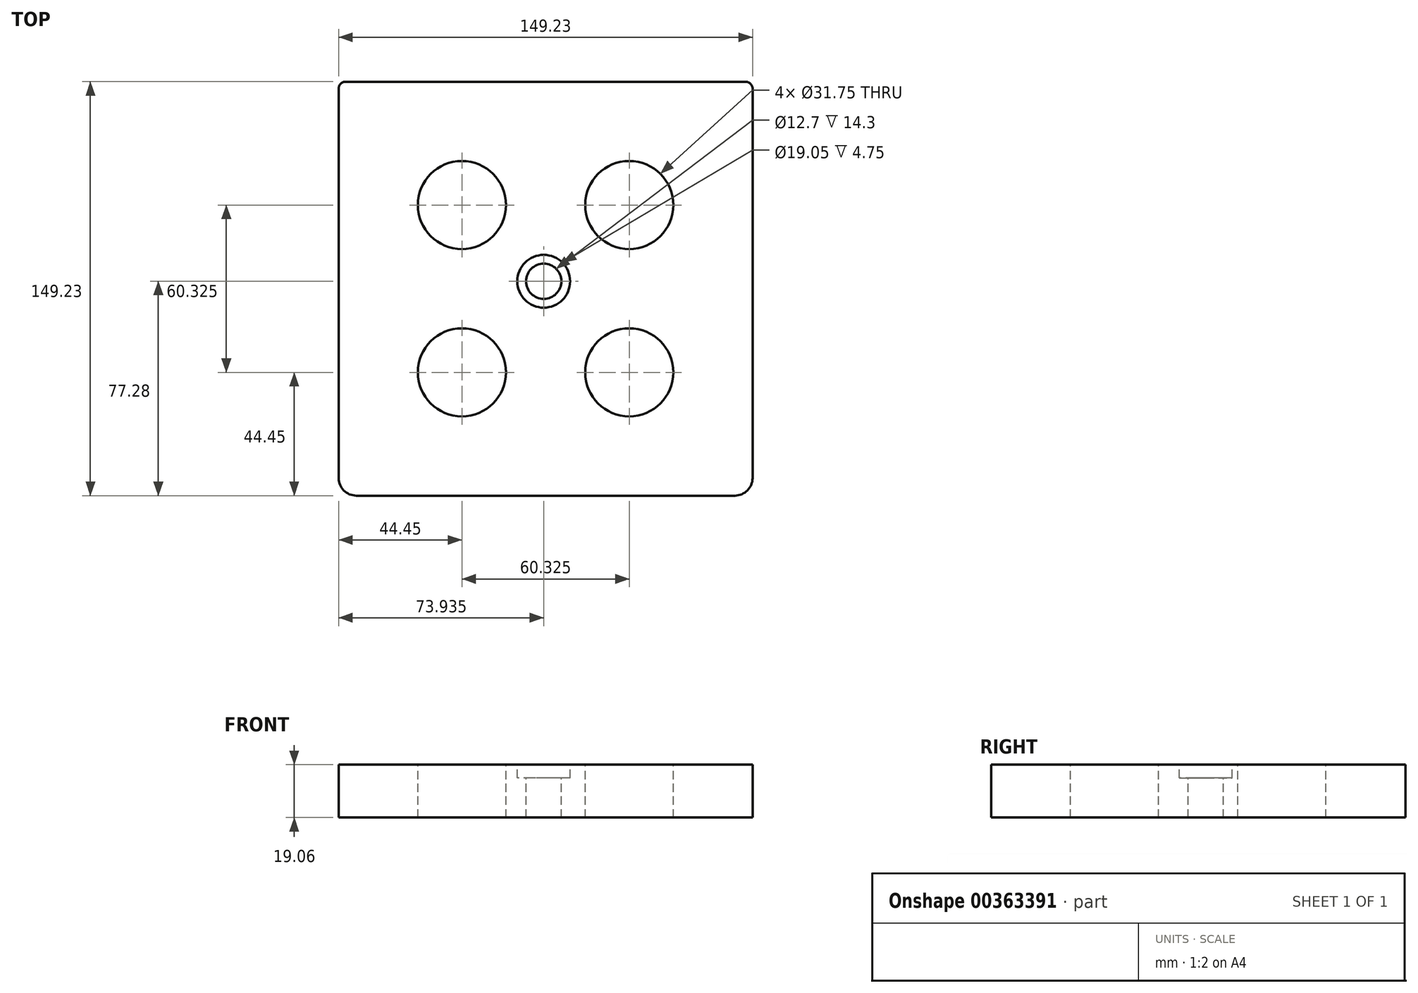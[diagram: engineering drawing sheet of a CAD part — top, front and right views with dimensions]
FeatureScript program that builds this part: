
annotation { "Feature Type Name" : "Feature", "Feature Type Description" : "" }
export const myFeature = defineFeature(function(context is Context, id is Id, definition is map)
    precondition{}
    {
        {
            var Q0;
            Q0=qCreatedBy(makeId("Top.planeOp"),FACE);
            var sketch = newSketch(context, id + "F0", { "sketchPlane" : qUnion([Q0])});
            skLineSegment(sketch, "E0.bottom", {"start": v(69.4, -77.28) * mm, "end": v(-67.12, -77.28) * mm});
            skLineSegment(sketch, "E0.top", {"start": v(73.22, 71.95) * mm, "end": v(-70.93, 71.95) * mm});
            skLineSegment(sketch, "E0.left", {"start": v(75.76, -70.93) * mm, "end": v(75.76, 69.4) * mm});
            skLineSegment(sketch, "E0.right", {"start": v(-73.47, -70.93) * mm, "end": v(-73.47, 69.4) * mm});
            skPoint(sketch, "E1.visualSharp", {"position": v(-73.47, 71.95) * mm});
            skArc(sketch, "E1.filletArc", {"start": v(-70.93, 71.95) * mm, "mid": v(-72.73, 71.2) * mm, "end": v(-73.47, 69.4) * mm});
            skPoint(sketch, "E2.visualSharp", {"position": v(75.76, 71.95) * mm});
            skArc(sketch, "E2.filletArc", {"start": v(75.76, 69.4) * mm, "mid": v(75.01, 71.2) * mm, "end": v(73.22, 71.95) * mm});
            skPoint(sketch, "E3.visualSharp", {"position": v(75.76, -77.28) * mm});
            skArc(sketch, "E3.filletArc", {"start": v(69.4, -77.28) * mm, "mid": v(73.9, -75.42) * mm, "end": v(75.76, -70.93) * mm});
            skPoint(sketch, "E4.visualSharp", {"position": v(-73.47, -77.28) * mm});
            skArc(sketch, "E4.filletArc", {"start": v(-73.47, -70.93) * mm, "mid": v(-71.6, -75.42) * mm, "end": v(-67.12, -77.28) * mm});
            skCircle(sketch, "E5", {"center": v(-29.02, 27.5) * mm, "radius": 15.88 * mm});
            skCircle(sketch, "E6", {"center": v(-29.02, -32.83) * mm, "radius": 15.88 * mm});
            skCircle(sketch, "E7", {"center": v(31.3, -32.83) * mm, "radius": 15.88 * mm});
            skCircle(sketch, "E8", {"center": v(31.3, 27.5) * mm, "radius": 15.88 * mm});
            skSolve(sketch);
        }
        {
            var Q0;
            Q0=makeQuery(id+"F0.imprint","IMPRINT",FACE,{"disambiguationData":[TD([[makeQuery(id+"F0.imprint","IMPRINT",EDGE,{"derivedFrom":sQuery(id+"F0.wireOp",EDGE,"E0.bottom")}),-1.0]])]});
            var Q1;
            Q1=sQuery(id+"F0.wireOp",EDGE,"DEAaRMsh-ce6J-Exax-naJt-bH9Wly1rZSn5");
            extrude(context, id + "F1", {"entities" : qUnion([Q0]), "surfaceEntities" : qUnion([Q1]), "endBound" : BoundingType.SYMMETRIC, "oppositeDirection" : true, "depth" : 19.05 * mm});
        }
        {
            var Q0;
            Q0=makeQuery(id+"F1.opExtrude","CAP_FACE",FACE,{"disambiguationData":[OSD([sQuery(id+"F0.wireOp",EDGE,"E0.bottom"),sQuery(id+"F0.wireOp",EDGE,"E0.top"),sQuery(id+"F0.wireOp",EDGE,"E0.left"),sQuery(id+"F0.wireOp",EDGE,"E0.right"),sQuery(id+"F0.wireOp",EDGE,"E1.filletArc"),sQuery(id+"F0.wireOp",EDGE,"E2.filletArc"),sQuery(id+"F0.wireOp",EDGE,"E3.filletArc"),sQuery(id+"F0.wireOp",EDGE,"E4.filletArc"),sQuery(id+"F0.wireOp",EDGE,"E5"),sQuery(id+"F0.wireOp",EDGE,"E6"),sQuery(id+"F0.wireOp",EDGE,"E7"),sQuery(id+"F0.wireOp",EDGE,"E8")])],"isStart":true});
            var sketch = newSketch(context, id + "F2", { "sketchPlane" : qUnion([Q0])});
            skCircle(sketch, "E9", {"center": v(0.46, 0) * mm, "radius": 6.35 * mm});
            skSolve(sketch);
        }
        {
            var Q0;
            Q0=sQuery(id+"F2.wireOp",VERTEX,"E9.center");
            var Q1;
            Q1=makeQuery(id+"F1.opExtrude","SWEPT_BODY",BODY,{"disambiguationData":[OSD([sQuery(id+"F0.wireOp",EDGE,"E0.bottom"),sQuery(id+"F0.wireOp",EDGE,"E0.top"),sQuery(id+"F0.wireOp",EDGE,"E0.left"),sQuery(id+"F0.wireOp",EDGE,"E0.right"),sQuery(id+"F0.wireOp",EDGE,"E1.filletArc"),sQuery(id+"F0.wireOp",EDGE,"E2.filletArc"),sQuery(id+"F0.wireOp",EDGE,"E3.filletArc"),sQuery(id+"F0.wireOp",EDGE,"E4.filletArc"),sQuery(id+"F0.wireOp",EDGE,"E5"),sQuery(id+"F0.wireOp",EDGE,"E6"),sQuery(id+"F0.wireOp",EDGE,"E7"),sQuery(id+"F0.wireOp",EDGE,"E8")])]});
            hole(context, id + "F3", {"style" : HoleStyle.C_BORE, "endStyle" : HoleEndStyle.THROUGH, "holeDiameter" : 12.7 * mm, "cBoreDiameter" : 19.05 * mm, "cBoreDepth" : 4.75 * mm, "majorDiameter" : 6.35 * mm, "isTappedThrough" : true, "tappedDepth" : 12.7 * mm, "tapClearance" : 3, "startFromSketch" : true, "locations" : qUnion([Q0]), "scope" : qUnion([Q1])});
        }
    });
